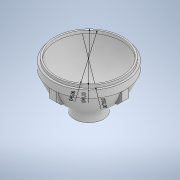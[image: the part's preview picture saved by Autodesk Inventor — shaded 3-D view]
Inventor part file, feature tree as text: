
AUTODESK INVENTOR PART (.ipt)
format: ipt  version: 2021 (Build 250183000, 183)  size: 273,920 bytes
history: native  units: mm
features: other x8, sketch x8, extrude x4, chamfer x1
ambient origin geometry x8: Origin, YZ Plane, XZ Plane, XY Plane, X Axis, Y Axis, Z Axis, Center Point
bodies: Solide2 (feature_tree)
feature tree (21):
  other  "Annotations"
  other  "Révolution1"
  extrude  "Extrusion1"  TaperAngle=90.0deg  [1 undecoded]
  extrude  "Extrusion2"  Depth=9.0mm
  extrude  "Extrusion3"  Depth=5.0mm
  extrude  "Trou creux extrusion"  Depth=50.0mm TaperAngle=0.0deg
  other  "Creuse Révolution"
  other  "Grand révolution cylindre"
  other  "Moyenne révolution dernier cylindre"
  chamfer  "Chanfrein1"  Distance=5.0mm
  sketch  "Esquisse1"
  sketch  "Esquisse2"
  sketch  "Esquisse3"
  sketch  "Esquisse4"
  sketch  "Esquisse5"
  sketch  "Esquisse6"
  sketch  "Esquisse9"
  sketch  "Esquisse11"
  other  "Cote de diamètre 3"
  other  "Cote de diamètre 4"
  other  "Cote de diamètre 5"
note: 1 required parameter value undecoded (feature->parameter linkage not recoverable at this tier; creation-order binding heuristic only, values carry confidence <= 0.55)
